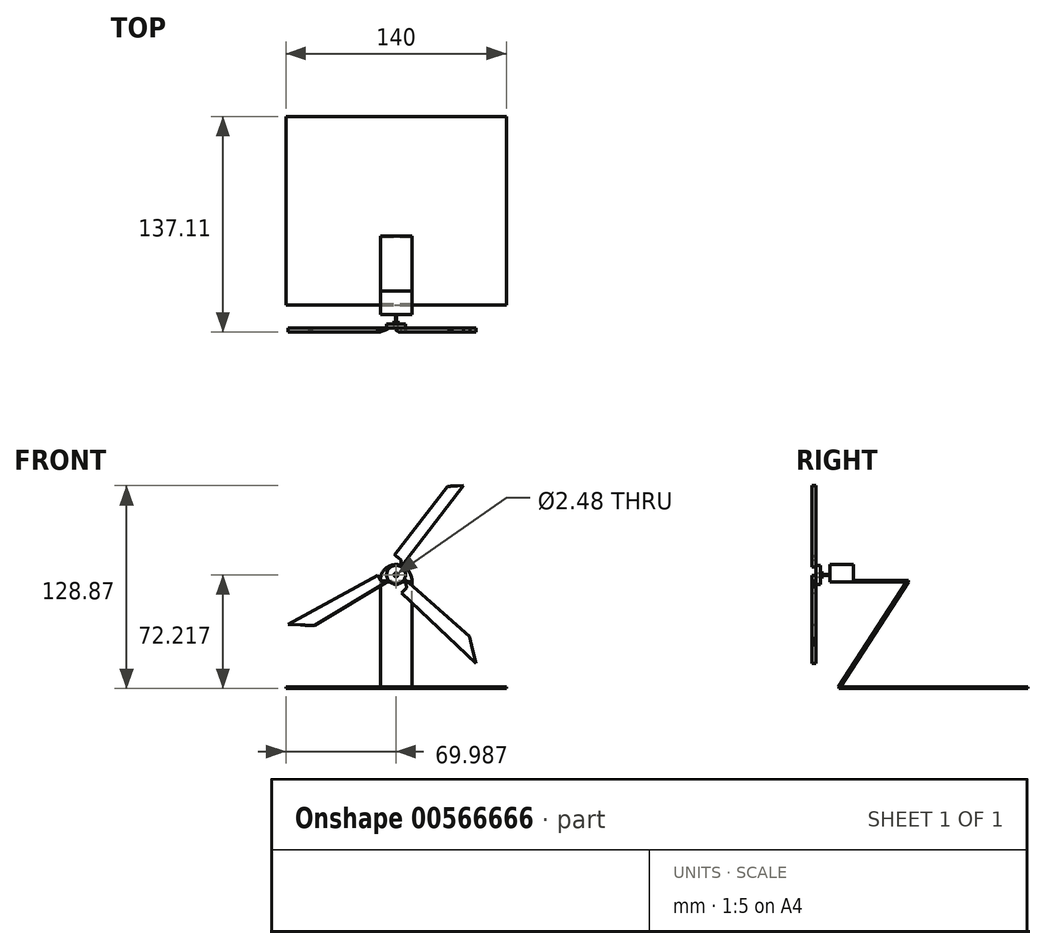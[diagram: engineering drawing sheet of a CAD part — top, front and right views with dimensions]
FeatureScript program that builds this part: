
annotation { "Feature Type Name" : "Feature", "Feature Type Description" : "" }
export const myFeature = defineFeature(function(context is Context, id is Id, definition is map)
    precondition{}
    {
        {
            var Q0;
            Q0=qCreatedBy(makeId("Top.planeOp"),FACE);
            var sketch = newSketch(context, id + "F0", { "sketchPlane" : qUnion([Q0])});
            skLineSegment(sketch, "E0.bottom", {"start": v(0, 0) * mm, "end": v(140, 0) * mm});
            skLineSegment(sketch, "E0.top", {"start": v(0, 120) * mm, "end": v(140, 120) * mm});
            skLineSegment(sketch, "E0.left", {"start": v(0, 0) * mm, "end": v(0, 120) * mm});
            skLineSegment(sketch, "E0.right", {"start": v(140, 0) * mm, "end": v(140, 120) * mm});
            skSolve(sketch);
        }
        {
            var Q0;
            Q0 = qSketchRegion(id + "F0", true);
            extrude(context, id + "F1", {"entities" : qUnion([Q0]), "depth" : 1 * mm, "offsetDistance" : 25 * mm});
        }
        {
            var Q0;
            Q0=qCreatedBy(makeId("Right.planeOp"),FACE);
            cPlane(context, id + "F2", {"entities" : qUnion([Q0]), "cplaneType" : CPlaneType.OFFSET, "offset" : 70 * mm, "width" : 150 * mm, "height" : 150 * mm});
        }
        {
            var Q0;
            Q0=qCreatedBy(id+"F2.planeOp",FACE);
            var sketch = newSketch(context, id + "F3", { "sketchPlane" : qUnion([Q0])});
            skLineSegment(sketch, "E1", {"start": v(0.77, 1.02) * mm, "end": v(43.74, 67.18) * mm});
            skLineSegment(sketch, "E2.0", {"start": v(-0.42, 1.02) * mm, "end": v(42.9, 67.73) * mm});
            skLineSegment(sketch, "E3", {"start": v(0.77, 1.02) * mm, "end": v(-0.42, 1.02) * mm});
            skLineSegment(sketch, "E4", {"start": v(42.9, 67.73) * mm, "end": v(44.1, 67.73) * mm});
            skLineSegment(sketch, "E5", {"start": v(43.74, 67.18) * mm, "end": v(44.1, 67.73) * mm});
            skSolve(sketch);
        }
        {
            var Q0;
            Q0 = qSketchRegion(id + "F3", true);
            extrude(context, id + "F4", {"entities" : qUnion([Q0]), "endBound" : BoundingType.SYMMETRIC, "depth" : 20 * mm, "offsetDistance" : 25 * mm});
        }
        {
            var Q0;
            Q0=makeQuery(id+"F4.opExtrude","SWEPT_FACE",FACE,{"disambiguationData":[OSD([sQuery(id+"F3.wireOp",EDGE,"E4")])]});
            var sketch = newSketch(context, id + "F5", { "sketchPlane" : qUnion([Q0])});
            skLineSegment(sketch, "E6.bottom", {"start": v(60, 44.1) * mm, "end": v(80, 44.1) * mm});
            skLineSegment(sketch, "E6.top", {"start": v(60, -5.9) * mm, "end": v(80, -5.9) * mm});
            skLineSegment(sketch, "E6.left", {"start": v(60, 44.1) * mm, "end": v(60, -5.9) * mm});
            skLineSegment(sketch, "E6.right", {"start": v(80, 44.1) * mm, "end": v(80, -5.9) * mm});
            skSolve(sketch);
        }
        {
            var Q0;
            Q0 = qSketchRegion(id + "F5", true);
            extrude(context, id + "F6", {"entities" : qUnion([Q0]), "operationType" : NewBodyOperationType.ADD, "depth" : 1 * mm, "offsetDistance" : 25 * mm});
        }
        {
            var Q0;
            Q0=makeQuery(id+"F6.opExtrude","SWEPT_FACE",FACE,{"disambiguationData":[OSD([sQuery(id+"F5.wireOp",EDGE,"E6.top")])]});
            var sketch = newSketch(context, id + "F7", { "sketchPlane" : qUnion([Q0])});
            skCircle(sketch, "E7", {"center": v(70, 68.73) * mm, "radius": 10 * mm});
            skSolve(sketch);
        }
        {
            var Q0;
            {var subQ1=sQuery(id+"F5.wireOp",EDGE,"E6.top");var subQ2=makeQuery(id+"F6.opExtrude","CAP_EDGE",EDGE,{"disambiguationData":[OSD([subQ1])],"isStart":false});Q0=makeQuery(id+"F7.imprint","IMPRINT",FACE,{"disambiguationData":[TD([[makeQuery(id+"F7.imprint","IMPRINT",EDGE,{"derivedFrom":subQ2}),1.0]])]});}
            extrude(context, id + "F8", {"entities" : qUnion([Q0]), "operationType" : NewBodyOperationType.ADD, "oppositeDirection" : true, "depth" : 15 * mm, "offsetDistance" : 25 * mm});
        }
        {
            var Q0;
            {var subQ0=sQuery(id+"F5.wireOp",EDGE,"E6.top");Q0=makeQuery(id+"F8.boolean.opBoolean","MERGE",FACE,{"derivedFrom":[makeQuery(id+"F6.opExtrude","SWEPT_FACE",FACE,{"disambiguationData":[OSD([subQ0])]}),makeQuery(id+"F8.opExtrude","CAP_FACE",FACE,{"disambiguationData":[OSD([subQ0,sQuery(id+"F7.wireOp",EDGE,"E7")])],"isStart":true})]});}
            var sketch = newSketch(context, id + "F9", { "sketchPlane" : qUnion([Q0])});
            skCircle(sketch, "E8", {"center": v(69.99, 72.22) * mm, "radius": 0.4 * mm});
            skSolve(sketch);
        }
        {
            var Q0;
            Q0 = qSketchRegion(id + "F9", true);
            extrude(context, id + "F10", {"entities" : qUnion([Q0]), "operationType" : NewBodyOperationType.ADD, "depth" : 4 * mm, "offsetDistance" : 25 * mm});
        }
        {
            var Q0;
            Q0=makeQuery(id+"F10.opExtrude","CAP_FACE",FACE,{"disambiguationData":[OSD([sQuery(id+"F9.wireOp",EDGE,"E8")])],"isStart":false});
            var sketch = newSketch(context, id + "F11", { "sketchPlane" : qUnion([Q0])});
            skCircle(sketch, "E9", {"center": v(69.99, 72.22) * mm, "radius": 1.24 * mm});
            skSolve(sketch);
        }
        {
            var Q0;
            Q0 = qSketchRegion(id + "F11", true);
            extrude(context, id + "F12", {"entities" : qUnion([Q0]), "operationType" : NewBodyOperationType.ADD, "depth" : 2 * mm, "offsetDistance" : 25 * mm});
        }
        {
            var Q0;
            Q0=makeQuery(id+"F12.opExtrude","CAP_FACE",FACE,{"disambiguationData":[OSD([sQuery(id+"F11.wireOp",EDGE,"E9")])],"isStart":false});
            var sketch = newSketch(context, id + "F13", { "sketchPlane" : qUnion([Q0])});
            skCircle(sketch, "E10", {"center": v(69.99, 72.22) * mm, "radius": 6 * mm});
            skSolve(sketch);
        }
        {
            var Q0;
            Q0=makeQuery(id+"F13.imprint","IMPRINT",FACE,{"disambiguationData":[TD([[makeQuery(id+"F13.imprint","IMPRINT",EDGE,{"derivedFrom":sQuery(id+"F13.wireOp",EDGE,"E10")}),1.0]])]});
            extrude(context, id + "F14", {"entities" : qUnion([Q0]), "depth" : 2.7 * mm, "offsetDistance" : 25 * mm});
        }
        {
            var Q0;
            Q0=makeQuery(id+"F14.opExtrude","CAP_FACE",FACE,{"disambiguationData":[OSD([sQuery(id+"F11.wireOp",EDGE,"E9"),sQuery(id+"F13.wireOp",EDGE,"E10")])],"isStart":false});
            var sketch = newSketch(context, id + "F15", { "sketchPlane" : qUnion([Q0])});
            skLineSegment(sketch, "E11", {"start": v(65.32, 68.45) * mm, "end": v(18.2, 40.09) * mm});
            skLineSegment(sketch, "E12", {"start": v(18.2, 40.09) * mm, "end": v(1.4, 40.59) * mm});
            skLineSegment(sketch, "E13", {"start": v(1.4, 40.59) * mm, "end": v(58.3, 72) * mm});
            skLineSegment(sketch, "E14", {"start": v(58.3, 72) * mm, "end": v(60.27, 68.45) * mm});
            skLineSegment(sketch, "E15", {"start": v(60.27, 68.45) * mm, "end": v(65.32, 68.45) * mm});
            skLineSegment(sketch, "E16", {"start": v(73.17, 77.3) * mm, "end": v(112.75, 128.87) * mm});
            skLineSegment(sketch, "E17", {"start": v(112.75, 128.87) * mm, "end": v(102.63, 128.46) * mm});
            skLineSegment(sketch, "E18", {"start": v(102.63, 128.46) * mm, "end": v(69.15, 84.83) * mm});
            skLineSegment(sketch, "E19", {"start": v(69.15, 84.83) * mm, "end": v(73.1, 81.79) * mm});
            skLineSegment(sketch, "E20", {"start": v(73.1, 81.79) * mm, "end": v(73.17, 77.3) * mm});
            skLineSegment(sketch, "E21", {"start": v(75.4, 69.63) * mm, "end": v(116.56, 33.15) * mm});
            skLineSegment(sketch, "E22", {"start": v(116.56, 33.15) * mm, "end": v(120.7, 15.95) * mm});
            skLineSegment(sketch, "E23", {"start": v(120.7, 15.95) * mm, "end": v(73.5, 60.65) * mm});
            skLineSegment(sketch, "E24", {"start": v(73.5, 60.65) * mm, "end": v(76.77, 64.1) * mm});
            skLineSegment(sketch, "E25", {"start": v(76.77, 64.1) * mm, "end": v(75.4, 69.63) * mm});
            skSolve(sketch);
        }
        {
            var Q0;
            Q0=makeQuery(id+"F15.imprint","IMPRINT",FACE,{"disambiguationData":[TD([[makeQuery(id+"F15.imprint","IMPRINT",EDGE,{"derivedFrom":sQuery(id+"F15.wireOp",EDGE,"E21")}),-1.0]])]});
            var Q1;
            Q1=makeQuery(id+"F15.imprint","IMPRINT",FACE,{"disambiguationData":[TD([[makeQuery(id+"F15.imprint","IMPRINT",EDGE,{"derivedFrom":sQuery(id+"F15.wireOp",EDGE,"E16")}),1.0]])]});
            var Q2;
            Q2=makeQuery(id+"F15.imprint","IMPRINT",FACE,{"disambiguationData":[TD([[makeQuery(id+"F15.imprint","IMPRINT",EDGE,{"derivedFrom":sQuery(id+"F15.wireOp",EDGE,"E11")}),-1.0]])]});
            extrude(context, id + "F16", {"entities" : qUnion([Q0, Q1, Q2]), "depth" : 2.5 * mm, "offsetDistance" : 25 * mm});
        }
        {
            var Q0;
            Q0=makeQuery(id+"F16.opExtrude","CAP_EDGE",EDGE,{"disambiguationData":[OSD([sQuery(id+"F15.wireOp",EDGE,"E11")])],"isStart":false});
            var Q1;
            Q1=makeQuery(id+"F16.opExtrude","CAP_EDGE",EDGE,{"disambiguationData":[OSD([sQuery(id+"F15.wireOp",EDGE,"E21")])],"isStart":false});
            var Q2;
            Q2=makeQuery(id+"F16.opExtrude","CAP_EDGE",EDGE,{"disambiguationData":[OSD([sQuery(id+"F15.wireOp",EDGE,"E18")])],"isStart":false});
            fillet(context, id + "F17", {"entities" : qUnion([Q0, Q1, Q2]), "radius" : 6 * mm, "tangentPropagation" : true, "allowEdgeOverflow" : false});
        }
    });
